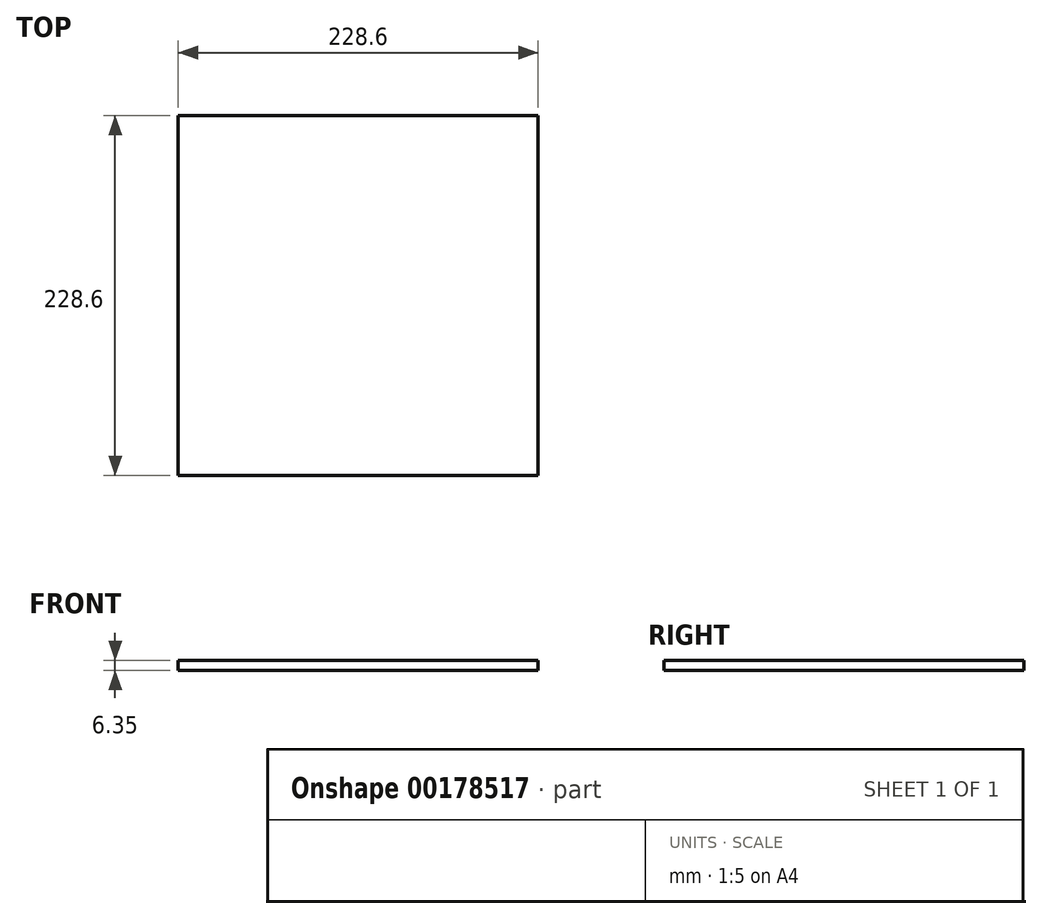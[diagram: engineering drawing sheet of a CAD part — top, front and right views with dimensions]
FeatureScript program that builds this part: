
annotation { "Feature Type Name" : "Feature", "Feature Type Description" : "" }
export const myFeature = defineFeature(function(context is Context, id is Id, definition is map)
    precondition{}
    {
        {
            var Q0;
            Q0=qCreatedBy(makeId("Top.planeOp"),FACE);
            var sketch = newSketch(context, id + "F0", { "sketchPlane" : qUnion([Q0])});
            skLineSegment(sketch, "E0.bottom", {"start": v(114.3, -114.3) * mm, "end": v(-114.3, -114.3) * mm});
            skLineSegment(sketch, "E0.top", {"start": v(114.3, 114.3) * mm, "end": v(-114.3, 114.3) * mm});
            skLineSegment(sketch, "E0.left", {"start": v(114.3, -114.3) * mm, "end": v(114.3, 114.3) * mm});
            skLineSegment(sketch, "E0.right", {"start": v(-114.3, -114.3) * mm, "end": v(-114.3, 114.3) * mm});
            skPoint(sketch, "E0.middle", {"position": v(0, 0) * mm});
            skSolve(sketch);
        }
        {
            var Q0;
            Q0=makeQuery(id+"F0.imprint","IMPRINT",FACE,{"disambiguationData":[TD([[makeQuery(id+"F0.imprint","IMPRINT",EDGE,{"derivedFrom":sQuery(id+"F0.wireOp",EDGE,"E0.bottom")}),-1.0]])]});
            extrude(context, id + "F1", {"entities" : qUnion([Q0]), "depth" : 6.35 * mm});
        }
    });
